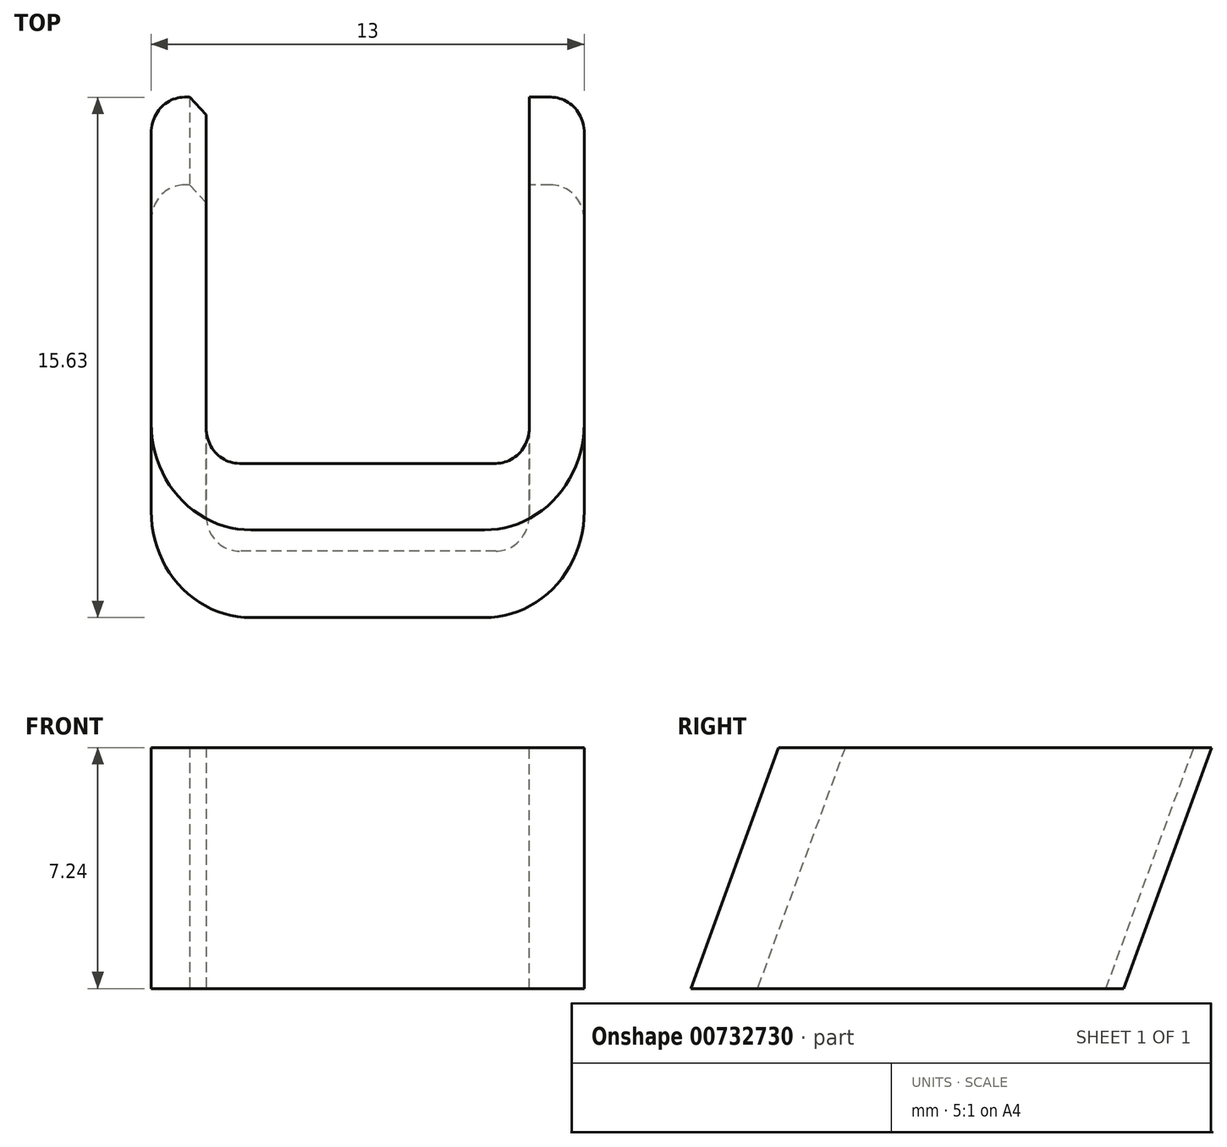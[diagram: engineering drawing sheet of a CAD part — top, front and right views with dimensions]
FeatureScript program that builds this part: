
annotation { "Feature Type Name" : "Feature", "Feature Type Description" : "" }
export const myFeature = defineFeature(function(context is Context, id is Id, definition is map)
    precondition{}
    {
        {
            var Q0;
            Q0=qCreatedBy(makeId("Right.planeOp"),FACE);
            var sketch = newSketch(context, id + "F0", { "sketchPlane" : qUnion([Q0])});
            skLineSegment(sketch, "E0", {"start": v(0, 0) * mm, "end": v(13, 0) * mm});
            skLineSegment(sketch, "E1", {"start": v(13, 0) * mm, "end": v(15.63, 7.24) * mm});
            skLineSegment(sketch, "E2", {"start": v(15.63, 7.24) * mm, "end": v(2.63, 7.24) * mm});
            skLineSegment(sketch, "E3", {"start": v(2.63, 7.24) * mm, "end": v(0, 0) * mm});
            skLineSegment(sketch, "E4", {"start": v(2.63, 7.24) * mm, "end": v(4.63, 7.24) * mm});
            skLineSegment(sketch, "E5", {"start": v(0, 0) * mm, "end": v(2, 0) * mm});
            skLineSegment(sketch, "E6", {"start": v(4.63, 7.24) * mm, "end": v(2, 0) * mm});
            skSolve(sketch);
        }
        {
            var Q0;
            {var subQ3=sQuery(id+"F0.wireOp",EDGE,"E3");var subQ7=sQuery(id+"F0.wireOp",EDGE,"E1");Q0=qUnion([makeQuery(id+"F0.imprint","IMPRINT",FACE,{"disambiguationData":[TD([[makeQuery(id+"F0.imprint","IMPRINT",EDGE,{"derivedFrom":subQ7}),1.0]])]}),makeQuery(id+"F0.imprint","IMPRINT",FACE,{"disambiguationData":[TD([[makeQuery(id+"F0.imprint","IMPRINT",EDGE,{"derivedFrom":subQ3}),1.0]])]})]);}
            extrude(context, id + "F1", {"entities" : qUnion([Q0]), "endBound" : BoundingType.SYMMETRIC, "depth" : 13 * mm, "offsetDistance" : 25 * mm});
        }
        {
            var Q0;
            {var subQ2=sQuery(id+"F0.wireOp",EDGE,"E1");Q0=makeQuery(id+"F0.imprint","IMPRINT",FACE,{"disambiguationData":[TD([[makeQuery(id+"F0.imprint","IMPRINT",EDGE,{"derivedFrom":subQ2}),1.0]])]});}
            extrude(context, id + "F2", {"entities" : qUnion([Q0]), "operationType" : NewBodyOperationType.REMOVE, "endBound" : BoundingType.SYMMETRIC, "depth" : 9.7 * mm, "offsetDistance" : 25 * mm});
        }
        {
            var Q0;
            Q0=makeQuery(id+"F2.boolean.opBoolean","COPY",EDGE,{"derivedFrom":makeQuery(id+"F2.opExtrude","CAP_EDGE",EDGE,{"disambiguationData":[OSD([sQuery(id+"F0.wireOp",EDGE,"E6")])],"isStart":false})});
            var Q1;
            Q1=makeQuery(id+"F2.boolean.opBoolean","COPY",EDGE,{"derivedFrom":makeQuery(id+"F2.opExtrude","CAP_EDGE",EDGE,{"disambiguationData":[OSD([sQuery(id+"F0.wireOp",EDGE,"E6")])],"isStart":true})});
            var Q2;
            Q2=makeQuery(id+"F1.opExtrude","CAP_EDGE",EDGE,{"disambiguationData":[OSD([sQuery(id+"F0.wireOp",EDGE,"E1")])],"isStart":true});
            var Q3;
            Q3=makeQuery(id+"F1.opExtrude","CAP_EDGE",EDGE,{"disambiguationData":[OSD([sQuery(id+"F0.wireOp",EDGE,"E1")])],"isStart":false});
            fillet(context, id + "F3", {"entities" : qUnion([Q0, Q1, Q2, Q3]), "radius" : 1 * mm, "tangentPropagation" : true, "allowEdgeOverflow" : false});
        }
        {
            var Q0;
            Q0=makeQuery(id+"F2.boolean.opBoolean","COPY",EDGE,{"derivedFrom":makeQuery(id+"F2.opExtrude","CAP_EDGE",EDGE,{"disambiguationData":[OSD([sQuery(id+"F0.wireOp",EDGE,"E1")])],"isStart":false})});
            var Q1;
            Q1=makeQuery(id+"F2.boolean.opBoolean","COPY",EDGE,{"derivedFrom":makeQuery(id+"F2.opExtrude","CAP_EDGE",EDGE,{"disambiguationData":[OSD([sQuery(id+"F0.wireOp",EDGE,"E1")])],"isStart":true})});
            chamfer(context, id + "F4", {"entities" : qUnion([Q0, Q1]), "width" : 0.5 * mm, "tangentPropagation" : true});
        }
        {
            var Q0;
            Q0=makeQuery(id+"F1.opExtrude","CAP_EDGE",EDGE,{"disambiguationData":[OSD([sQuery(id+"F0.wireOp",EDGE,"E3")])],"isStart":false});
            var Q1;
            Q1=makeQuery(id+"F1.opExtrude","CAP_EDGE",EDGE,{"disambiguationData":[OSD([sQuery(id+"F0.wireOp",EDGE,"E3")])],"isStart":true});
            fillet(context, id + "F5", {"entities" : qUnion([Q0, Q1]), "radius" : 3 * mm, "tangentPropagation" : true, "allowEdgeOverflow" : false});
        }
    });
